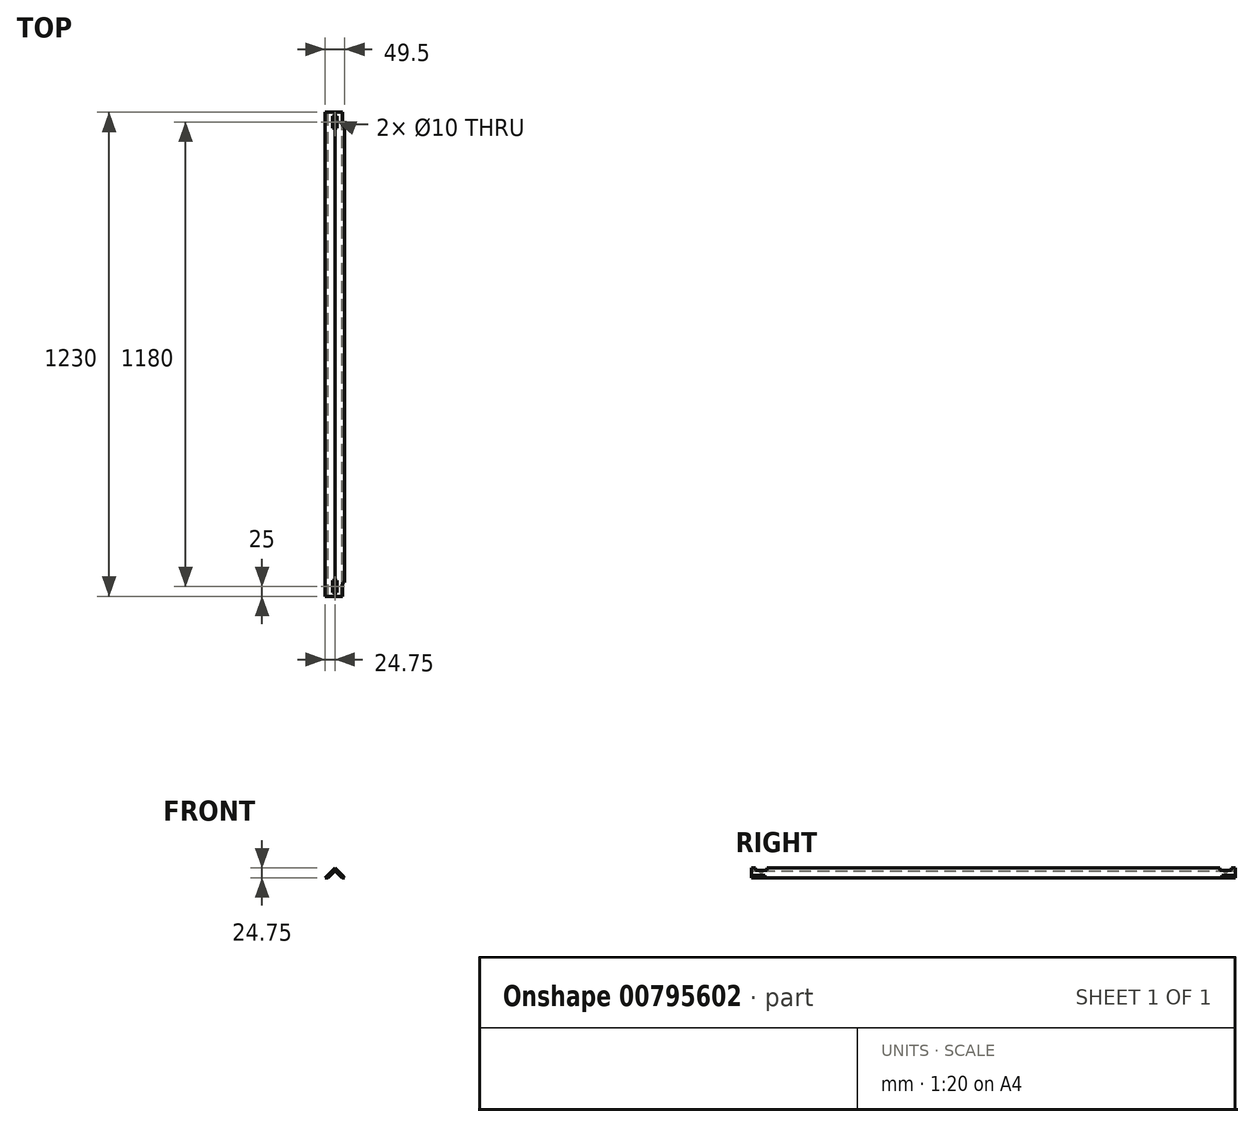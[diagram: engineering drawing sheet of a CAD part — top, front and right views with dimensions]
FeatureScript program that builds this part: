
annotation { "Feature Type Name" : "Feature", "Feature Type Description" : "" }
export const myFeature = defineFeature(function(context is Context, id is Id, definition is map)
    precondition{}
    {
        {
            var Q0;
            Q0=qCreatedBy(makeId("Front.planeOp"),FACE);
            var sketch = newSketch(context, id + "F0", { "sketchPlane" : qUnion([Q0])});
            skLineSegment(sketch, "E0.top", {"start": v(24.75, 0) * mm, "end": v(0, 24.75) * mm});
            skLineSegment(sketch, "E0.right", {"start": v(-24.75, 0) * mm, "end": v(0, 24.75) * mm});
            skPoint(sketch, "E0.middle", {"position": v(0, 0) * mm});
            skLineSegment(sketch, "E1", {"start": v(-17.68, 0) * mm, "end": v(0, 17.68) * mm});
            skLineSegment(sketch, "E2", {"start": v(0, 17.68) * mm, "end": v(17.68, 0) * mm});
            skLineSegment(sketch, "E3", {"start": v(-24.75, 0) * mm, "end": v(-17.68, 0) * mm});
            skLineSegment(sketch, "E4", {"start": v(24.75, 0) * mm, "end": v(17.68, 0) * mm});
            skSolve(sketch);
        }
        {
            var Q0;
            Q0=makeQuery(id+"F0.imprint","IMPRINT",FACE,{"disambiguationData":[TD([[makeQuery(id+"F0.imprint","IMPRINT",EDGE,{"derivedFrom":sQuery(id+"F0.wireOp",EDGE,"E0.top")}),1.0]])]});
            extrude(context, id + "F1", {"entities" : qUnion([Q0]), "endBound" : BoundingType.SYMMETRIC, "depth" : 1230 * mm, "offsetDistance" : 25 * mm});
        }
        {
            var Q0;
            Q0=qCreatedBy(makeId("Right.planeOp"),FACE);
            cPlane(context, id + "F2", {"entities" : qUnion([Q0]), "cplaneType" : CPlaneType.OFFSET, "offset" : 30 * mm, "width" : 150 * mm, "height" : 150 * mm});
        }
        {
            var Q0;
            Q0=qCreatedBy(id+"F2.planeOp",FACE);
            var sketch = newSketch(context, id + "F3", { "sketchPlane" : qUnion([Q0])});
            skLineSegment(sketch, "E5.bottom", {"start": v(-605, 24.75) * mm, "end": v(-575, 24.75) * mm});
            skLineSegment(sketch, "E5.top", {"start": v(-605, 18.75) * mm, "end": v(-575, 18.75) * mm});
            skLineSegment(sketch, "E5.left", {"start": v(-605, 24.75) * mm, "end": v(-605, 18.75) * mm});
            skLineSegment(sketch, "E5.right", {"start": v(-575, 24.75) * mm, "end": v(-575, 18.75) * mm});
            skLineSegment(sketch, "E6.MirrorCS", {"start": v(605, 18.75) * mm, "end": v(575, 18.75) * mm});
            skLineSegment(sketch, "E7.MirrorCS", {"start": v(575, 24.75) * mm, "end": v(575, 18.75) * mm});
            skLineSegment(sketch, "E8.MirrorCS", {"start": v(605, 24.75) * mm, "end": v(575, 24.75) * mm});
            skLineSegment(sketch, "E9.MirrorCS", {"start": v(605, 24.75) * mm, "end": v(605, 18.75) * mm});
            skSolve(sketch);
        }
        {
            var Q0;
            Q0=makeQuery(id+"F3.imprint","IMPRINT",FACE,{"disambiguationData":[TD([[makeQuery(id+"F3.imprint","IMPRINT",EDGE,{"derivedFrom":sQuery(id+"F3.wireOp",EDGE,"E6.MirrorCS")}),-1.0]])]});
            var Q1;
            Q1=makeQuery(id+"F3.imprint","IMPRINT",FACE,{"disambiguationData":[TD([[makeQuery(id+"F3.imprint","IMPRINT",EDGE,{"derivedFrom":sQuery(id+"F3.wireOp",EDGE,"E5.bottom")}),-1.0]])]});
            extrude(context, id + "F4", {"entities" : qUnion([Q0, Q1]), "operationType" : NewBodyOperationType.REMOVE, "endBound" : BoundingType.THROUGH_ALL, "oppositeDirection" : true, "depth" : 25 * mm, "offsetDistance" : 25 * mm});
        }
        {
            var Q0;
            Q0=makeQuery(id+"F4.boolean.opBoolean","COPY",FACE,{"derivedFrom":makeQuery(id+"F4.opExtrude","SWEPT_FACE",FACE,{"disambiguationData":[OSD([sQuery(id+"F3.wireOp",EDGE,"E5.top")])]})});
            var sketch = newSketch(context, id + "F5", { "sketchPlane" : qUnion([Q0])});
            skCircle(sketch, "E10", {"center": v(0, -590) * mm, "radius": 5 * mm});
            skCircle(sketch, "E11.MirrorC", {"center": v(0, 590) * mm, "radius": 5 * mm});
            skLineSegment(sketch, "E12", {"start": v(6, -590) * mm, "end": v(-6, -590) * mm, "construction": true});
            skLineSegment(sketch, "E13", {"start": v(-6, -605) * mm, "end": v(-6, -575) * mm, "construction": true});
            skLineSegment(sketch, "E14", {"start": v(-6, -575) * mm, "end": v(6, -575) * mm, "construction": true});
            skSolve(sketch);
        }
        {
            var Q0;
            Q0=sQuery(id+"F5.wireOp",VERTEX,"E10.center");
            var Q1;
            Q1=sQuery(id+"F5.wireOp",VERTEX,"E11.MirrorC.center");
            var Q2;
            Q2=makeQuery(id+"F1.opExtrude","SWEPT_BODY",BODY,{"disambiguationData":[OSD([sQuery(id+"F0.wireOp",EDGE,"E0.top"),sQuery(id+"F0.wireOp",EDGE,"E0.right"),sQuery(id+"F0.wireOp",EDGE,"E1"),sQuery(id+"F0.wireOp",EDGE,"E2"),sQuery(id+"F0.wireOp",EDGE,"E3"),sQuery(id+"F0.wireOp",EDGE,"E4")])]});
            hole(context, id + "F6", {"style" : HoleStyle.SIMPLE, "endStyle" : HoleEndStyle.THROUGH, "standardTappedOrClearance" : lookupTablePath({ "standard" : "ISO", "size" : "10", "type" : "Drilled" }), "standardBlindInLast" : lookupTablePath({ "standard" : "ISO", "size" : "10", "type" : "Drilled" }), "holeDiameter" : 10 * mm, "majorDiameter" : 5 * mm, "isTappedThrough" : true, "tappedDepth" : 12.7 * mm, "tapClearance" : 3, "locations" : qUnion([Q0, Q1]), "scope" : qUnion([Q2])});
        }
        {
            var Q0;
            Q0=makeQuery(id+"F1.opExtrude","SWEPT_FACE",FACE,{"disambiguationData":[OSD([sQuery(id+"F0.wireOp",EDGE,"E0.top")])]});
            var sketch = newSketch(context, id + "F7", { "sketchPlane" : qUnion([Q0])});
            skLineSegment(sketch, "E15.bottom", {"start": v(-615, -17.5) * mm, "end": v(-580, -17.5) * mm});
            skLineSegment(sketch, "E15.top", {"start": v(-615, -9.5) * mm, "end": v(-580, -9.5) * mm});
            skLineSegment(sketch, "E15.left", {"start": v(-615, -17.5) * mm, "end": v(-615, -9.5) * mm});
            skLineSegment(sketch, "E15.right", {"start": v(-580, -17.5) * mm, "end": v(-580, -9.5) * mm});
            skLineSegment(sketch, "E16.MirrorCS", {"start": v(615, -17.5) * mm, "end": v(580, -17.5) * mm});
            skLineSegment(sketch, "E17.MirrorCS", {"start": v(615, -9.5) * mm, "end": v(580, -9.5) * mm});
            skLineSegment(sketch, "E18.MirrorCS", {"start": v(580, -17.5) * mm, "end": v(580, -9.5) * mm});
            skLineSegment(sketch, "E19.MirrorCS", {"start": v(615, -17.5) * mm, "end": v(615, -9.5) * mm});
            skSolve(sketch);
        }
        {
            var Q0;
            Q0=makeQuery(id+"F7.imprint","IMPRINT",FACE,{"disambiguationData":[TD([[makeQuery(id+"F7.imprint","IMPRINT",EDGE,{"derivedFrom":sQuery(id+"F7.wireOp",EDGE,"E15.bottom")}),1.0]])]});
            var Q1;
            Q1=makeQuery(id+"F7.imprint","IMPRINT",FACE,{"disambiguationData":[TD([[makeQuery(id+"F7.imprint","IMPRINT",EDGE,{"derivedFrom":sQuery(id+"F7.wireOp",EDGE,"E16.MirrorCS")}),1.0]])]});
            extrude(context, id + "F8", {"entities" : qUnion([Q0, Q1]), "operationType" : NewBodyOperationType.REMOVE, "oppositeDirection" : true, "depth" : 25 * mm, "offsetDistance" : 25 * mm});
        }
    });
